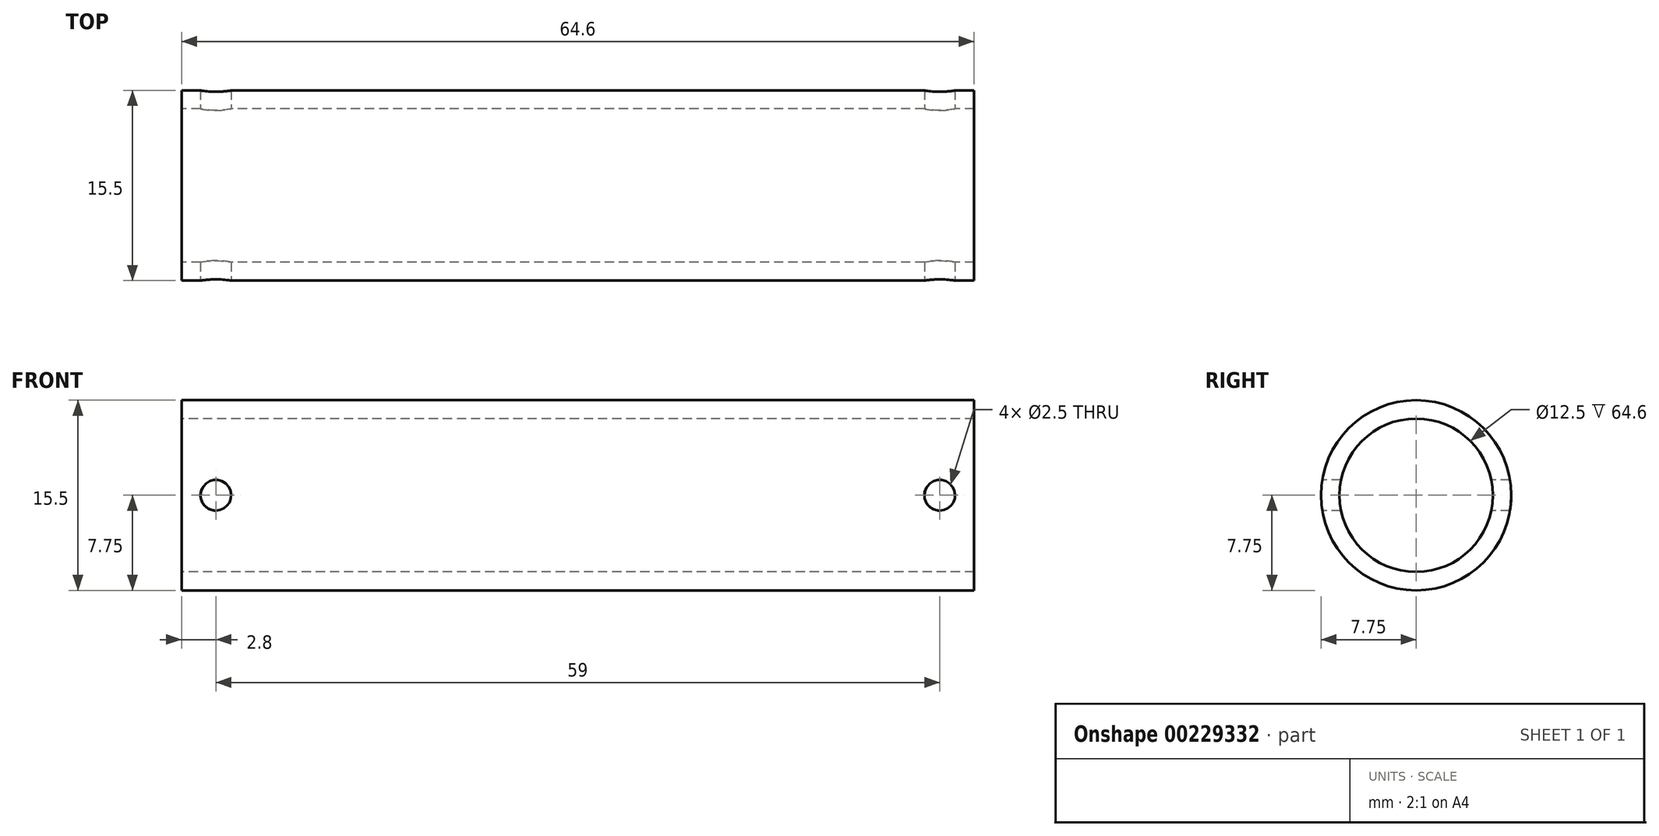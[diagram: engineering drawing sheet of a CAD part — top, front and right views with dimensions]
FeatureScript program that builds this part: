
annotation { "Feature Type Name" : "Feature", "Feature Type Description" : "" }
export const myFeature = defineFeature(function(context is Context, id is Id, definition is map)
    precondition{}
    {
        {
            var Q0;
            Q0=qCreatedBy(makeId("Right.planeOp"),FACE);
            var sketch = newSketch(context, id + "F0", { "sketchPlane" : qUnion([Q0])});
            skCircle(sketch, "E0", {"center": v(0, 0) * mm, "radius": 6.25 * mm});
            skCircle(sketch, "E1", {"center": v(0, 0) * mm, "radius": 7.75 * mm});
            skSolve(sketch);
        }
        {
            var Q0;
            Q0 = qSketchRegion(id + "F0", true);
            extrude(context, id + "F1", {"entities" : qUnion([Q0]), "depth" : 64.6 * mm, "symmetric" : true});
        }
        {
            var Q0;
            Q0=qCreatedBy(makeId("Front.planeOp"),FACE);
            var sketch = newSketch(context, id + "F2", { "sketchPlane" : qUnion([Q0])});
            skCircle(sketch, "E2", {"center": v(-29.5, 0) * mm, "radius": 1.25 * mm});
            skCircle(sketch, "E3", {"center": v(29.5, 0) * mm, "radius": 1.25 * mm});
            skSolve(sketch);
        }
        {
            var Q0;
            Q0 = qSketchRegion(id + "F2", true);
            extrude(context, id + "F3", {"entities" : qUnion([Q0]), "operationType" : NewBodyOperationType.REMOVE, "oppositeDirection" : true, "depth" : 25 * mm, "symmetric" : true});
        }
    });
